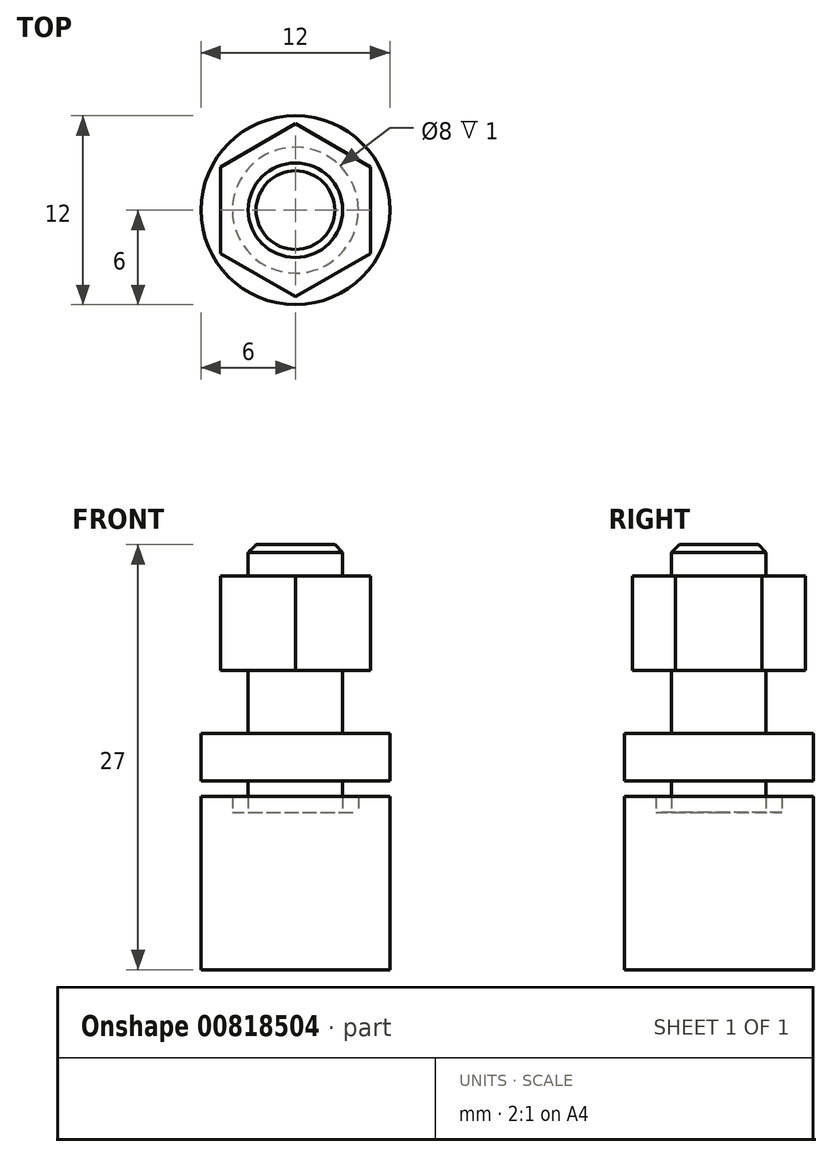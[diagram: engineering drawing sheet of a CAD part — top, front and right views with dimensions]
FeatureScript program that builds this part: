
annotation { "Feature Type Name" : "Feature", "Feature Type Description" : "" }
export const myFeature = defineFeature(function(context is Context, id is Id, definition is map)
    precondition{}
    {
        {
            var Q0;
            Q0=qCreatedBy(makeId("Front.planeOp"),FACE);
            var sketch = newSketch(context, id + "F0", { "sketchPlane" : qUnion([Q0])});
            skLineSegment(sketch, "E0", {"start": v(0, 8) * mm, "end": v(-2.5, 8) * mm});
            skLineSegment(sketch, "E1", {"start": v(-2.5, 8) * mm, "end": v(-3, 7.5) * mm});
            skLineSegment(sketch, "E2", {"start": v(-3, 7.5) * mm, "end": v(-3, 6) * mm});
            skLineSegment(sketch, "E3", {"start": v(-3, 6) * mm, "end": v(-5.5, 6) * mm});
            skLineSegment(sketch, "E4", {"start": v(-5.5, 6) * mm, "end": v(-5.5, 0) * mm});
            skLineSegment(sketch, "E5", {"start": v(-5.5, 0) * mm, "end": v(-3, 0) * mm});
            skLineSegment(sketch, "E6", {"start": v(-3, 0) * mm, "end": v(-3, -4) * mm});
            skLineSegment(sketch, "E7", {"start": v(-3, -4) * mm, "end": v(-6, -4) * mm});
            skLineSegment(sketch, "E8", {"start": v(-6, -4) * mm, "end": v(-6, -7) * mm});
            skLineSegment(sketch, "E9", {"start": v(-6, -7) * mm, "end": v(-3, -7) * mm});
            skLineSegment(sketch, "E10", {"start": v(-3, -7) * mm, "end": v(-3, -9) * mm});
            skLineSegment(sketch, "E11", {"start": v(-3, -9) * mm, "end": v(-4, -9) * mm});
            skLineSegment(sketch, "E12", {"start": v(-4, -9) * mm, "end": v(-4, -8) * mm});
            skLineSegment(sketch, "E13", {"start": v(-4, -8) * mm, "end": v(-6, -8) * mm});
            skLineSegment(sketch, "E14", {"start": v(-6, -8) * mm, "end": v(-6, -19) * mm});
            skLineSegment(sketch, "E15", {"start": v(-6, -19) * mm, "end": v(0, -19) * mm});
            skLineSegment(sketch, "E16.MirrorCS", {"start": v(2.5, 8) * mm, "end": v(3, 7.5) * mm, "construction": true});
            skLineSegment(sketch, "E17.MirrorCS", {"start": v(3, 7.5) * mm, "end": v(3, 6) * mm, "construction": true});
            skLineSegment(sketch, "E18.MirrorCS", {"start": v(3, -9) * mm, "end": v(4, -9) * mm, "construction": true});
            skLineSegment(sketch, "E19.MirrorCS", {"start": v(6, -19) * mm, "end": v(0, -19) * mm, "construction": true});
            skLineSegment(sketch, "E20.MirrorCS", {"start": v(0, 8) * mm, "end": v(2.5, 8) * mm, "construction": true});
            skLineSegment(sketch, "E21.MirrorCS", {"start": v(6, -8) * mm, "end": v(6, -19) * mm, "construction": true});
            skLineSegment(sketch, "E22.MirrorCS", {"start": v(4, -8) * mm, "end": v(6, -8) * mm, "construction": true});
            skLineSegment(sketch, "E23.MirrorCS", {"start": v(4, -9) * mm, "end": v(4, -8) * mm, "construction": true});
            skLineSegment(sketch, "E24.MirrorCS", {"start": v(3, 6) * mm, "end": v(5.5, 6) * mm, "construction": true});
            skLineSegment(sketch, "E25.MirrorCS", {"start": v(3, -4) * mm, "end": v(6, -4) * mm, "construction": true});
            skLineSegment(sketch, "E26.MirrorCS", {"start": v(6, -4) * mm, "end": v(6, -7) * mm, "construction": true});
            skLineSegment(sketch, "E27.MirrorCS", {"start": v(5.5, 6) * mm, "end": v(5.5, 0) * mm, "construction": true});
            skLineSegment(sketch, "E28.MirrorCS", {"start": v(3, 0) * mm, "end": v(3, -4) * mm, "construction": true});
            skLineSegment(sketch, "E29.MirrorCS", {"start": v(5.5, 0) * mm, "end": v(3, 0) * mm, "construction": true});
            skLineSegment(sketch, "E30.MirrorCS", {"start": v(3, -7) * mm, "end": v(3, -9) * mm, "construction": true});
            skLineSegment(sketch, "E31.MirrorCS", {"start": v(6, -7) * mm, "end": v(3, -7) * mm, "construction": true});
            skLineSegment(sketch, "E32", {"start": v(0, -19) * mm, "end": v(0, 8) * mm});
            skSolve(sketch);
        }
        {
            var Q0;
            Q0=qSketchRegion(id+"F0",true);
            var Q1;
            Q1=sQuery(id+"F0.wireOp",EDGE,"E32");
            revolve(context, id + "F1", {"entities" : qUnion([Q0]), "axis" : qUnion([Q1]), "revolveType" : RevolveType.FULL});
        }
        {
            var Q0;
            Q0=makeQuery(id+"F1.opRevolve","SWEPT_FACE",FACE,{"disambiguationData":[OSD([sQuery(id+"F0.wireOp",EDGE,"E3")])]});
            var sketch = newSketch(context, id + "F2", { "sketchPlane" : qUnion([Q0])});
            skCircle(sketch, "E33.cCircle", {"center": v(0, 0) * mm, "radius": 5.5 * mm, "construction": true});
            skLineSegment(sketch, "E33.0", {"start": v(0, 5.5) * mm, "end": v(4.76, 2.75) * mm});
            skLineSegment(sketch, "E33.1", {"start": v(4.76, 2.75) * mm, "end": v(4.76, -2.75) * mm});
            skLineSegment(sketch, "E33.2", {"start": v(4.76, -2.75) * mm, "end": v(0, -5.5) * mm});
            skLineSegment(sketch, "E33.3", {"start": v(0, -5.5) * mm, "end": v(-4.76, -2.75) * mm});
            skLineSegment(sketch, "E33.4", {"start": v(-4.76, -2.75) * mm, "end": v(-4.76, 2.75) * mm});
            skLineSegment(sketch, "E33.5", {"start": v(-4.76, 2.75) * mm, "end": v(0, 5.5) * mm});
            skSolve(sketch);
        }
        {
            var Q0;
            {var subQ0=sQuery(id+"F2.wireOp",EDGE,"E33.4");Q0=makeQuery(id+"F2.imprint","IMPRINT",FACE,{"disambiguationData":[TD([[makeQuery(id+"F2.imprint","IMPRINT",EDGE,{"derivedFrom":subQ0}),1.0]])]});}
            var Q1;
            {var subQ0=sQuery(id+"F2.wireOp",EDGE,"E33.3");Q1=makeQuery(id+"F2.imprint","IMPRINT",FACE,{"disambiguationData":[TD([[makeQuery(id+"F2.imprint","IMPRINT",EDGE,{"derivedFrom":subQ0}),1.0]])]});}
            var Q2;
            {var subQ0=sQuery(id+"F2.wireOp",EDGE,"E33.2");Q2=makeQuery(id+"F2.imprint","IMPRINT",FACE,{"disambiguationData":[TD([[makeQuery(id+"F2.imprint","IMPRINT",EDGE,{"derivedFrom":subQ0}),1.0]])]});}
            var Q3;
            {var subQ0=sQuery(id+"F2.wireOp",EDGE,"E33.1");Q3=makeQuery(id+"F2.imprint","IMPRINT",FACE,{"disambiguationData":[TD([[makeQuery(id+"F2.imprint","IMPRINT",EDGE,{"derivedFrom":subQ0}),1.0]])]});}
            var Q4;
            {var subQ0=sQuery(id+"F2.wireOp",EDGE,"E33.0");Q4=makeQuery(id+"F2.imprint","IMPRINT",FACE,{"disambiguationData":[TD([[makeQuery(id+"F2.imprint","IMPRINT",EDGE,{"derivedFrom":subQ0}),1.0]])]});}
            var Q5;
            {var subQ0=sQuery(id+"F2.wireOp",EDGE,"E33.5");Q5=makeQuery(id+"F2.imprint","IMPRINT",FACE,{"disambiguationData":[TD([[makeQuery(id+"F2.imprint","IMPRINT",EDGE,{"derivedFrom":subQ0}),1.0]])]});}
            extrude(context, id + "F3", {"entities" : qUnion([Q0, Q1, Q2, Q3, Q4, Q5]), "operationType" : NewBodyOperationType.REMOVE, "endBound" : BoundingType.UP_TO_NEXT, "oppositeDirection" : true, "depth" : 25 * mm});
        }
    });
